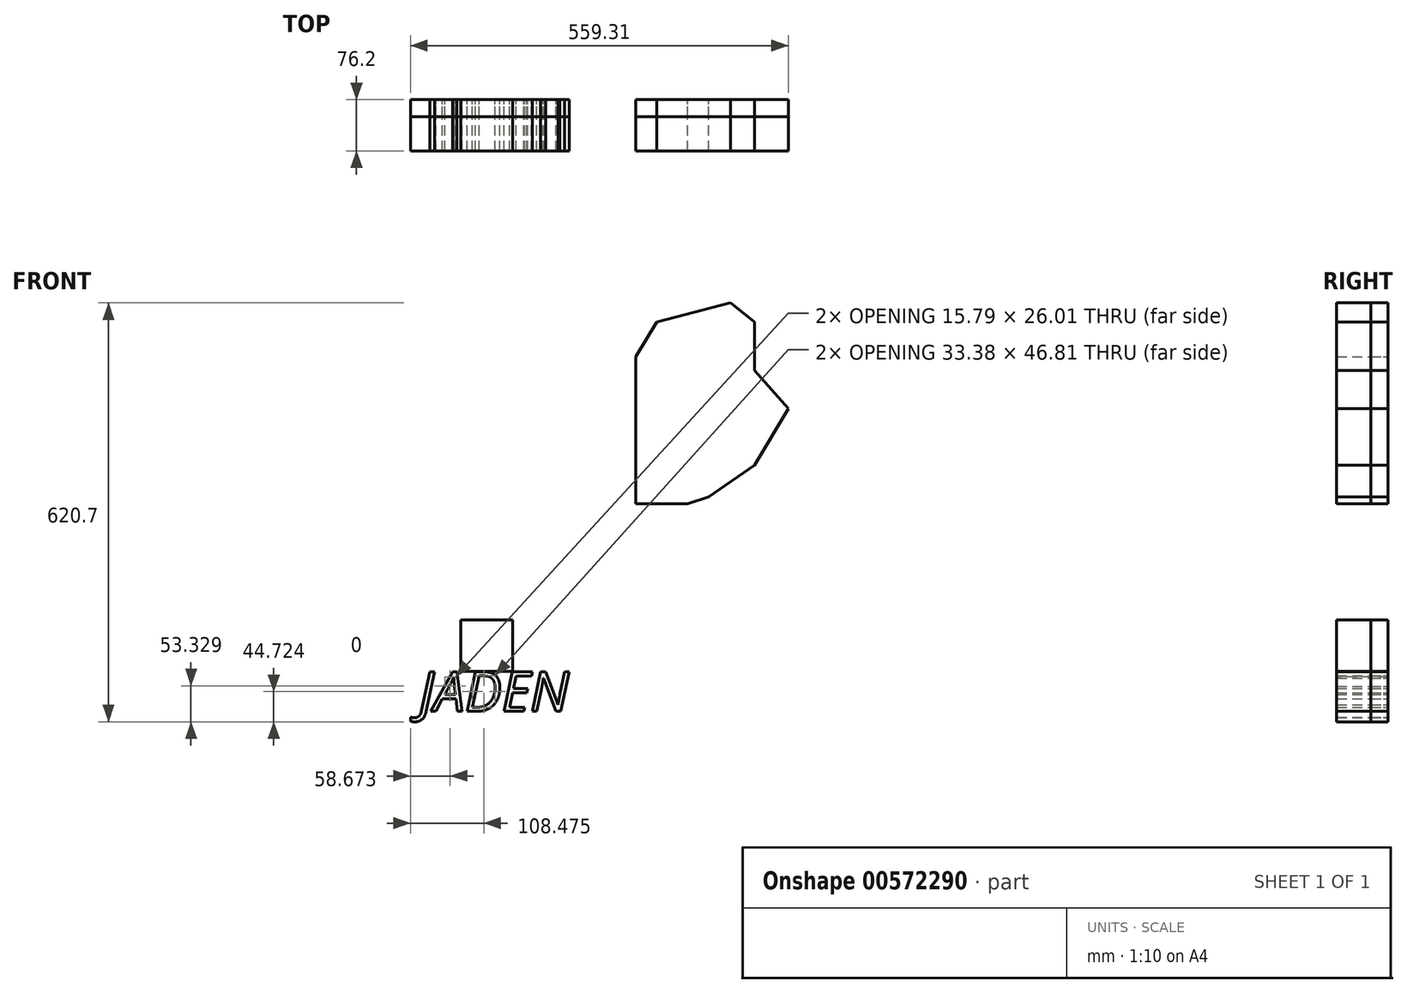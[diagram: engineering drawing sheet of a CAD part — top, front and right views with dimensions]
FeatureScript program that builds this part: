
annotation { "Feature Type Name" : "Feature", "Feature Type Description" : "" }
export const myFeature = defineFeature(function(context is Context, id is Id, definition is map)
    precondition{}
    {
        {
            var Q0;
            Q0=qCreatedBy(makeId("Front.planeOp"),FACE);
            var sketch = newSketch(context, id + "F0", { "sketchPlane" : qUnion([Q0])});
            skLineSegment(sketch, "E0.bottom", {"start": v(-76.2, 76.2) * mm, "end": v(0, 76.2) * mm});
            skLineSegment(sketch, "E0.top", {"start": v(-76.2, 0) * mm, "end": v(0, 0) * mm});
            skLineSegment(sketch, "E0.left", {"start": v(-76.2, 76.2) * mm, "end": v(-76.2, 0) * mm});
            skLineSegment(sketch, "E0.right", {"start": v(0, 76.2) * mm, "end": v(0, 0) * mm});
            skText(sketch, "E1", { "text": "JADEN", "fontName": "OpenSans-Italic.ttf"});
            skPoint(sketch, "E2", {"position": v(-38.1, 0) * mm});
            skLineSegment(sketch, "E3", {"start": v(58.63, 95.77) * mm, "end": v(134.83, 95.77) * mm});
            skLineSegment(sketch, "E4", {"start": v(134.83, 95.77) * mm, "end": v(134.83, 19.57) * mm});
            skLineSegment(sketch, "E5", {"start": v(134.83, 19.57) * mm, "end": v(211.03, 19.57) * mm});
            skLineSegment(sketch, "E6", {"start": v(58.63, 95.77) * mm, "end": v(58.63, 128.9) * mm});
            skLineSegment(sketch, "E7", {"start": v(59.03, 128.95) * mm, "end": v(135.23, 128.95) * mm});
            skLineSegment(sketch, "E8", {"start": v(135.23, 128.95) * mm, "end": v(211.43, 128.95) * mm});
            skLineSegment(sketch, "E9", {"start": v(186.2, 128.95) * mm, "end": v(207.4, 128.95) * mm});
            skLineSegment(sketch, "E10", {"start": v(207.4, 128.95) * mm, "end": v(207.4, 52.75) * mm});
            skLineSegment(sketch, "E11", {"start": v(182.73, 409.13) * mm, "end": v(182.73, 332.93) * mm});
            skLineSegment(sketch, "E12", {"start": v(182.73, 332.93) * mm, "end": v(259.33, 332.93) * mm});
            skLineSegment(sketch, "E13", {"start": v(259.33, 332.93) * mm, "end": v(259.33, 248.65) * mm});
            skLineSegment(sketch, "E14", {"start": v(259.33, 248.65) * mm, "end": v(290.39, 258.6) * mm});
            skLineSegment(sketch, "E15", {"start": v(290.39, 258.6) * mm, "end": v(290.39, 290.94) * mm});
            skLineSegment(sketch, "E16", {"start": v(290.39, 290.94) * mm, "end": v(290.39, 342.12) * mm});
            skLineSegment(sketch, "E17", {"start": v(290.39, 342.12) * mm, "end": v(358.7, 376.34) * mm});
            skLineSegment(sketch, "E18", {"start": v(358.7, 376.34) * mm, "end": v(358.7, 445.93) * mm});
            skLineSegment(sketch, "E19", {"start": v(358.7, 445.93) * mm, "end": v(322.82, 414.97) * mm});
            skLineSegment(sketch, "E20", {"start": v(322.82, 414.97) * mm, "end": v(322.82, 376.34) * mm});
            skLineSegment(sketch, "E21", {"start": v(322.82, 376.34) * mm, "end": v(213.78, 346.92) * mm});
            skLineSegment(sketch, "E22", {"start": v(213.78, 346.92) * mm, "end": v(213.78, 384.59) * mm});
            skLineSegment(sketch, "E23", {"start": v(213.78, 384.59) * mm, "end": v(182.73, 409.13) * mm});
            skLineSegment(sketch, "E24", {"start": v(182.73, 409.13) * mm, "end": v(182.73, 466.57) * mm});
            skLineSegment(sketch, "E25", {"start": v(213.78, 384.59) * mm, "end": v(213.78, 474.1) * mm});
            skLineSegment(sketch, "E26", {"start": v(322.82, 414.97) * mm, "end": v(322.82, 506.38) * mm});
            skLineSegment(sketch, "E27", {"start": v(358.7, 445.93) * mm, "end": v(358.7, 517.82) * mm});
            skLineSegment(sketch, "E28", {"start": v(182.73, 466.57) * mm, "end": v(213.78, 517.82) * mm});
            skLineSegment(sketch, "E29", {"start": v(358.7, 517.82) * mm, "end": v(322.82, 546.17) * mm});
            skLineSegment(sketch, "E30", {"start": v(213.78, 474.1) * mm, "end": v(213.78, 517.82) * mm});
            skLineSegment(sketch, "E31", {"start": v(322.82, 506.38) * mm, "end": v(322.82, 546.17) * mm});
            skLineSegment(sketch, "E32", {"start": v(322.82, 546.17) * mm, "end": v(213.78, 517.82) * mm});
            skLineSegment(sketch, "E33", {"start": v(290.39, 258.6) * mm, "end": v(358.7, 305.63) * mm});
            skLineSegment(sketch, "E34", {"start": v(358.7, 305.63) * mm, "end": v(358.7, 376.34) * mm});
            skLineSegment(sketch, "E35", {"start": v(259.33, 248.65) * mm, "end": v(182.73, 248.65) * mm});
            skLineSegment(sketch, "E36", {"start": v(182.73, 248.65) * mm, "end": v(182.73, 332.93) * mm});
            skLineSegment(sketch, "E37", {"start": v(358.7, 376.34) * mm, "end": v(408.37, 389.73) * mm});
            skLineSegment(sketch, "E38", {"start": v(358.7, 305.63) * mm, "end": v(408.37, 389.73) * mm});
            skLineSegment(sketch, "E39", {"start": v(358.7, 445.93) * mm, "end": v(408.37, 389.73) * mm});
            const initialGuessF0  = {"E1": [-0.13815, -0.0591, 1, 0, 0.0591]};
            skSetInitialGuess(sketch, initialGuessF0);
            skSolve(sketch);
        }
        {
            var Q0;
            Q0 = qSketchRegion(id + "F0", true);
            extrude(context, id + "F1", {"entities" : qUnion([Q0]), "depth" : 76.2 * mm, "offsetDistance" : 25.4 * mm});
        }
        {
            var Q0;
            Q0 = qSketchRegion(id + "F0", true);
            extrude(context, id + "F2", {"entities" : qUnion([Q0]), "depth" : 25.4 * mm, "offsetDistance" : 25.4 * mm});
        }
    });
